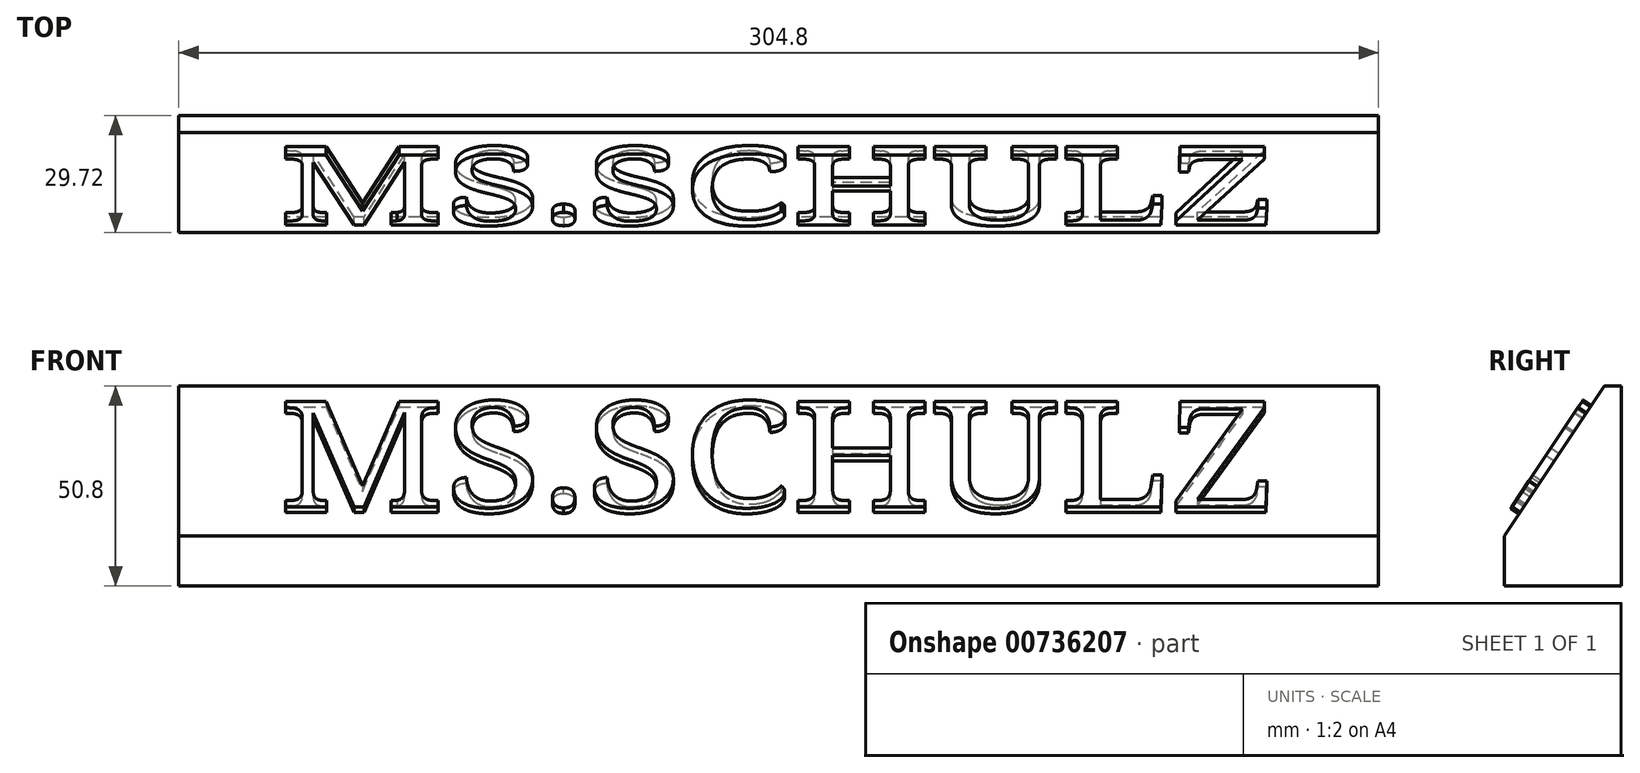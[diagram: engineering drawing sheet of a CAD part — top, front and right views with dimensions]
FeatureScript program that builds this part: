
annotation { "Feature Type Name" : "Feature", "Feature Type Description" : "" }
export const myFeature = defineFeature(function(context is Context, id is Id, definition is map)
    precondition{}
    {
        {
            var Q0;
            Q0=qCreatedBy(makeId("Top.planeOp"),FACE);
            var sketch = newSketch(context, id + "F0", { "sketchPlane" : qUnion([Q0])});
            skLineSegment(sketch, "E0.bottom", {"start": v(-114.23, 33.11) * mm, "end": v(190.57, 33.11) * mm});
            skLineSegment(sketch, "E0.top", {"start": v(-114.23, -17.69) * mm, "end": v(190.57, -17.69) * mm});
            skLineSegment(sketch, "E0.left", {"start": v(-114.23, 33.11) * mm, "end": v(-114.23, -17.69) * mm});
            skLineSegment(sketch, "E0.right", {"start": v(190.57, 33.11) * mm, "end": v(190.57, -17.69) * mm});
            skSolve(sketch);
        }
        {
            var Q0;
            Q0=makeQuery(id+"F0.imprint","IMPRINT",FACE,{"disambiguationData":[TD([[makeQuery(id+"F0.imprint","IMPRINT",EDGE,{"derivedFrom":sQuery(id+"F0.wireOp",EDGE,"E0.bottom")}),-1.0]])]});
            extrude(context, id + "F1", {"entities" : qUnion([Q0]), "depth" : 50.8 * mm, "offsetDistance" : 25.4 * mm});
        }
        {
            var Q0;
            Q0=makeQuery(id+"F1.opExtrude","SWEPT_FACE",FACE,{"disambiguationData":[OSD([sQuery(id+"F0.wireOp",EDGE,"E0.left")])]});
            var sketch = newSketch(context, id + "F2", { "sketchPlane" : qUnion([Q0])});
            skLineSegment(sketch, "E1", {"start": v(-7.71, 50.8) * mm, "end": v(17.69, 50.8) * mm});
            skLineSegment(sketch, "E2", {"start": v(17.69, 50.8) * mm, "end": v(17.69, 25.4) * mm});
            skLineSegment(sketch, "E3", {"start": v(17.69, 25.4) * mm, "end": v(17.69, 38.1) * mm});
            skLineSegment(sketch, "E4", {"start": v(17.69, 38.1) * mm, "end": v(17.69, 50.8) * mm});
            skLineSegment(sketch, "E5", {"start": v(4.99, 50.8) * mm, "end": v(-7.71, 50.8) * mm});
            skLineSegment(sketch, "E6", {"start": v(17.69, 25.4) * mm, "end": v(17.69, 0) * mm});
            skLineSegment(sketch, "E7", {"start": v(17.69, 0) * mm, "end": v(17.69, 12.7) * mm});
            skLineSegment(sketch, "E8", {"start": v(17.69, 12.7) * mm, "end": v(17.69, 25.4) * mm});
            skLineSegment(sketch, "E9", {"start": v(-7.71, 50.8) * mm, "end": v(17.69, 12.7) * mm});
            skSolve(sketch);
        }
        {
            var Q0;
            Q0=makeQuery(id+"F2.imprint","IMPRINT",FACE,{"disambiguationData":[TD([[makeQuery(id+"F2.imprint","IMPRINT",EDGE,{"derivedFrom":sQuery(id+"F2.wireOp",EDGE,"E1")}),-1.0]])]});
            extrude(context, id + "F3", {"entities" : qUnion([Q0]), "operationType" : NewBodyOperationType.REMOVE, "endBound" : BoundingType.THROUGH_ALL, "oppositeDirection" : true, "depth" : 25.4 * mm, "offsetDistance" : 25.4 * mm});
        }
        {
            var Q0;
            Q0=makeQuery(id+"F3.boolean.opBoolean","COPY",FACE,{"derivedFrom":makeQuery(id+"F3.opExtrude","SWEPT_FACE",FACE,{"disambiguationData":[OSD([sQuery(id+"F2.wireOp",EDGE,"E9")])]})});
            var sketch = newSketch(context, id + "F4", { "sketchPlane" : qUnion([Q0])});
            skText(sketch, "E10", { "text": "MS.SCHULZ", "fontName": "NotoSerif-Regular.ttf"});
            const initialGuessF4  = {"E10": [-0.08883, 0.00796, 1, 0, 0.03244]};
            skSetInitialGuess(sketch, initialGuessF4);
            skSolve(sketch);
        }
        {
            var Q0;
            Q0 = qSketchRegion(id + "F4", true);
            extrude(context, id + "F5", {"entities" : qUnion([Q0]), "operationType" : NewBodyOperationType.ADD, "depth" : 2.54 * mm, "offsetDistance" : 25.4 * mm});
        }
        {
            var Q0;
            Q0=makeQuery(id+"F1.opExtrude","SWEPT_FACE",FACE,{"disambiguationData":[OSD([sQuery(id+"F0.wireOp",EDGE,"E0.bottom")])]});
            extrude(context, id + "F6", {"entities" : qUnion([Q0]), "operationType" : NewBodyOperationType.REMOVE, "oppositeDirection" : true, "depth" : 21.08 * mm, "offsetDistance" : 25.4 * mm});
        }
    });
